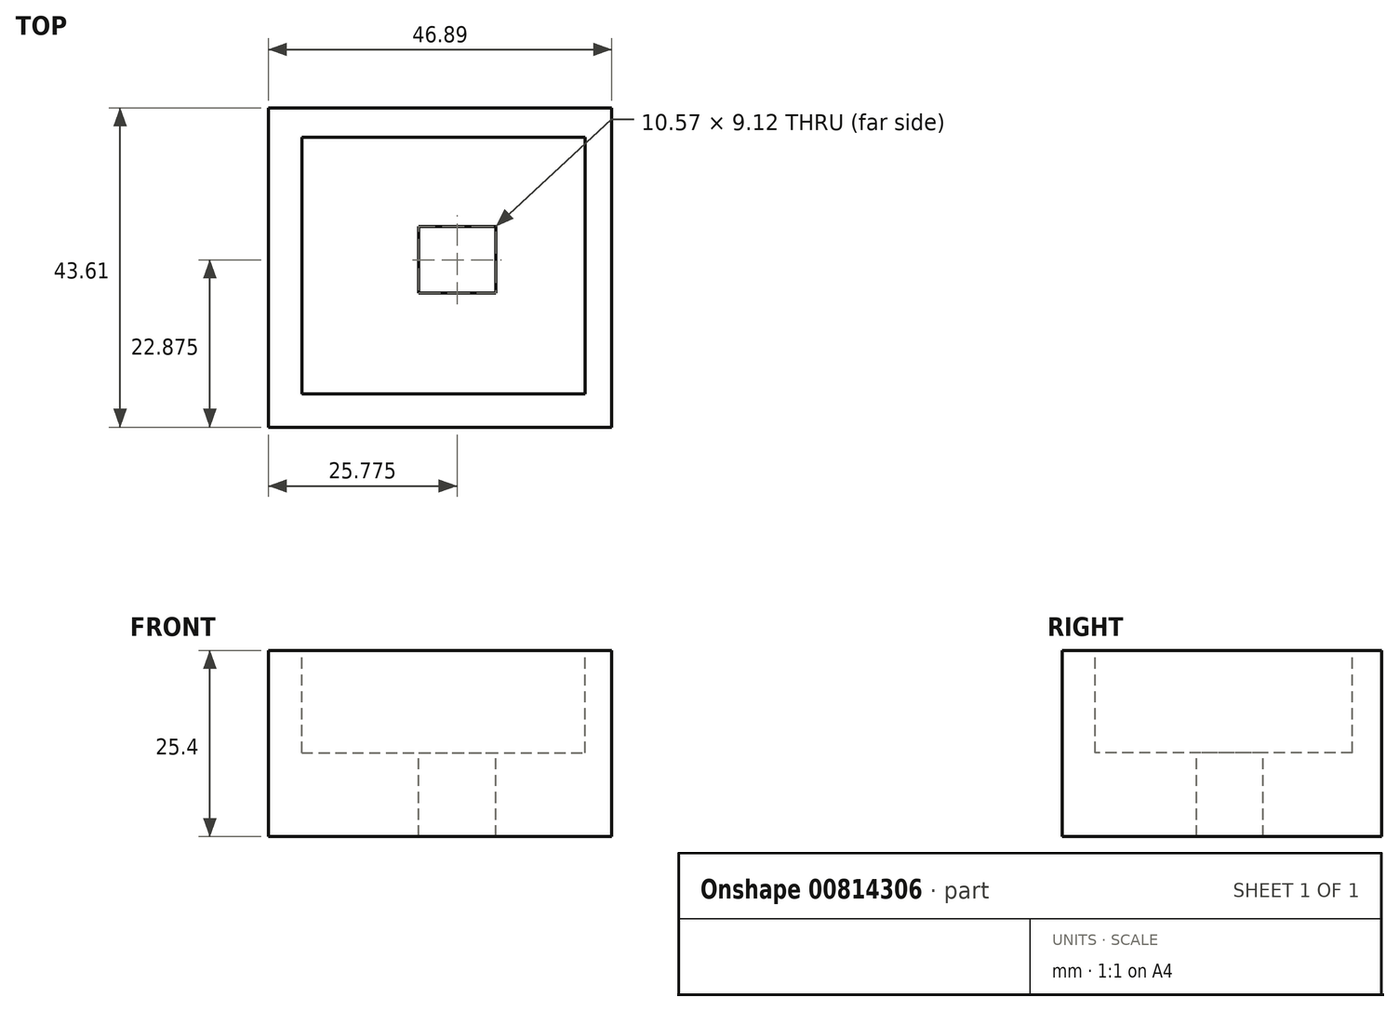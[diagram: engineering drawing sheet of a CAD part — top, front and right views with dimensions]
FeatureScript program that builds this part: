
annotation { "Feature Type Name" : "Feature", "Feature Type Description" : "" }
export const myFeature = defineFeature(function(context is Context, id is Id, definition is map)
    precondition{}
    {
        {
            var Q0;
            Q0=qCreatedBy(makeId("Top.planeOp"),FACE);
            var sketch = newSketch(context, id + "F0", { "sketchPlane" : qUnion([Q0])});
            skLineSegment(sketch, "E0.bottom", {"start": v(-39.42, 36.1) * mm, "end": v(7.47, 36.1) * mm});
            skLineSegment(sketch, "E0.top", {"start": v(-39.42, -7.51) * mm, "end": v(7.47, -7.51) * mm});
            skLineSegment(sketch, "E0.left", {"start": v(-39.42, 36.1) * mm, "end": v(-39.42, -7.51) * mm});
            skLineSegment(sketch, "E0.right", {"start": v(7.47, 36.1) * mm, "end": v(7.47, -7.51) * mm});
            skSolve(sketch);
        }
        {
            var Q0;
            Q0=makeQuery(id+"F0.imprint","IMPRINT",FACE,{"disambiguationData":[TD([[makeQuery(id+"F0.imprint","IMPRINT",EDGE,{"derivedFrom":sQuery(id+"F0.wireOp",EDGE,"E0.bottom")}),-1.0]])]});
            extrude(context, id + "F1", {"entities" : qUnion([Q0]), "depth" : 25.4 * mm, "offsetDistance" : 25.4 * mm});
        }
        {
            var Q0;
            Q0=makeQuery(id+"F1.opExtrude","CAP_FACE",FACE,{"disambiguationData":[OSD([sQuery(id+"F0.wireOp",EDGE,"E0.bottom"),sQuery(id+"F0.wireOp",EDGE,"E0.top"),sQuery(id+"F0.wireOp",EDGE,"E0.left"),sQuery(id+"F0.wireOp",EDGE,"E0.right")])],"isStart":false});
            var sketch = newSketch(context, id + "F2", { "sketchPlane" : qUnion([Q0])});
            skLineSegment(sketch, "E1.bottom", {"start": v(-34.85, 32.1) * mm, "end": v(3.84, 32.1) * mm});
            skLineSegment(sketch, "E1.top", {"start": v(-34.85, -2.98) * mm, "end": v(3.84, -2.98) * mm});
            skLineSegment(sketch, "E1.left", {"start": v(-34.85, 32.1) * mm, "end": v(-34.85, -2.98) * mm});
            skLineSegment(sketch, "E1.right", {"start": v(3.84, 32.1) * mm, "end": v(3.84, -2.98) * mm});
            skSolve(sketch);
        }
        {
            var Q0;
            Q0=makeQuery(id+"F2.imprint","IMPRINT",FACE,{"disambiguationData":[TD([[makeQuery(id+"F2.imprint","IMPRINT",EDGE,{"derivedFrom":sQuery(id+"F2.wireOp",EDGE,"E1.bottom")}),-1.0]])]});
            extrude(context, id + "F3", {"entities" : qUnion([Q0]), "operationType" : NewBodyOperationType.REMOVE, "oppositeDirection" : true, "depth" : 13.97 * mm, "offsetDistance" : 25.4 * mm});
        }
        {
            var Q0;
            Q0=makeQuery(id+"F3.boolean.opBoolean","COPY",FACE,{"derivedFrom":makeQuery(id+"F3.opExtrude","CAP_FACE",FACE,{"disambiguationData":[OSD([sQuery(id+"F2.wireOp",EDGE,"E1.bottom"),sQuery(id+"F2.wireOp",EDGE,"E1.top"),sQuery(id+"F2.wireOp",EDGE,"E1.left"),sQuery(id+"F2.wireOp",EDGE,"E1.right")])],"isStart":false})});
            var sketch = newSketch(context, id + "F4", { "sketchPlane" : qUnion([Q0])});
            skLineSegment(sketch, "E2.bottom", {"start": v(-18.93, 19.92) * mm, "end": v(-8.36, 19.92) * mm});
            skLineSegment(sketch, "E2.top", {"start": v(-18.93, 10.8) * mm, "end": v(-8.36, 10.8) * mm});
            skLineSegment(sketch, "E2.left", {"start": v(-18.93, 19.92) * mm, "end": v(-18.93, 10.8) * mm});
            skLineSegment(sketch, "E2.right", {"start": v(-8.36, 19.92) * mm, "end": v(-8.36, 10.8) * mm});
            skSolve(sketch);
        }
        {
            var Q0;
            Q0 = qSketchRegion(id + "F4", true);
            extrude(context, id + "F5", {"entities" : qUnion([Q0]), "operationType" : NewBodyOperationType.REMOVE, "oppositeDirection" : true, "depth" : 25.4 * mm, "offsetDistance" : 25.4 * mm});
        }
    });
